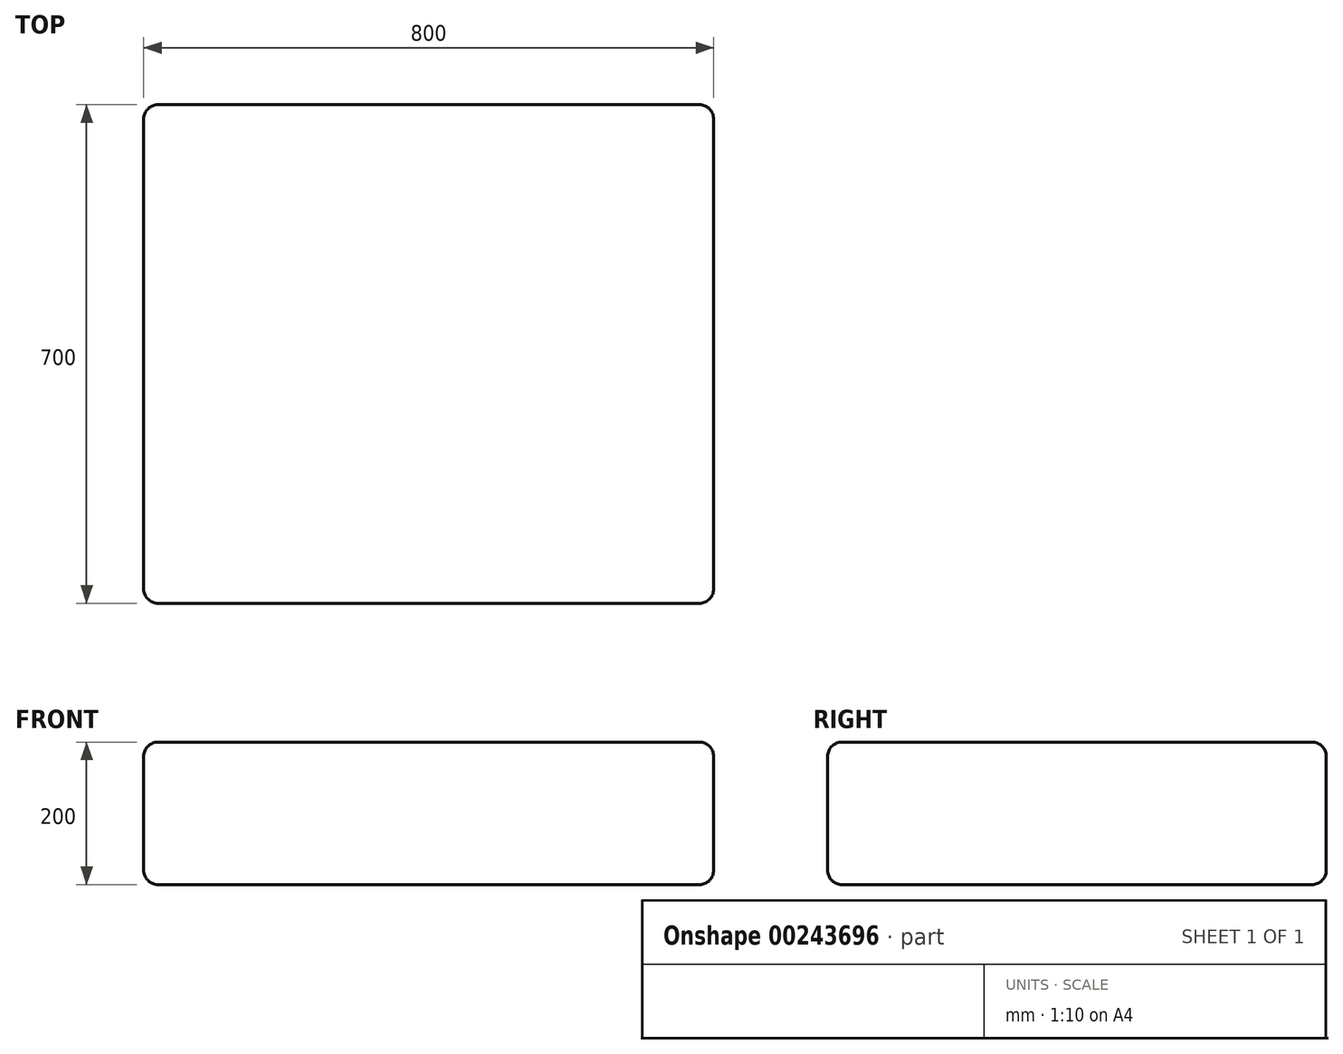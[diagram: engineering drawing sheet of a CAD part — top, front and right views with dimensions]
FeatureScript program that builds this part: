
annotation { "Feature Type Name" : "Feature", "Feature Type Description" : "" }
export const myFeature = defineFeature(function(context is Context, id is Id, definition is map)
    precondition{}
    {
        {
            var Q0;
            Q0=qCreatedBy(makeId("Top.planeOp"),FACE);
            var sketch = newSketch(context, id + "F0", { "sketchPlane" : qUnion([Q0])});
            skLineSegment(sketch, "E0.bottom", {"start": v(-400, 350) * mm, "end": v(400, 350) * mm});
            skLineSegment(sketch, "E0.top", {"start": v(-400, -350) * mm, "end": v(400, -350) * mm});
            skLineSegment(sketch, "E0.left", {"start": v(-400, 350) * mm, "end": v(-400, -350) * mm});
            skLineSegment(sketch, "E0.right", {"start": v(400, 350) * mm, "end": v(400, -350) * mm});
            skLineSegment(sketch, "E1", {"start": v(0, 350) * mm, "end": v(0, -350) * mm, "construction": true});
            skLineSegment(sketch, "E2", {"start": v(-400, 0) * mm, "end": v(400, 0) * mm, "construction": true});
            skSolve(sketch);
        }
        {
            var Q0;
            Q0=makeQuery(id+"F0.imprint","IMPRINT",FACE,{"disambiguationData":[TD([[makeQuery(id+"F0.imprint","IMPRINT",EDGE,{"derivedFrom":sQuery(id+"F0.wireOp",EDGE,"E0.bottom")}),-1.0]])]});
            extrude(context, id + "F1", {"entities" : qUnion([Q0]), "endBound" : BoundingType.SYMMETRIC, "depth" : 200 * mm});
        }
        {
            var Q0;
            Q0=makeQuery(id+"F1.opExtrude","SWEPT_EDGE",EDGE,{"disambiguationData":[OSD([sQuery(id+"F0.wireOp",EDGE,"E0.top"),sQuery(id+"F0.wireOp",EDGE,"E0.left")])]});
            var Q1;
            Q1=makeQuery(id+"F1.opExtrude","SWEPT_EDGE",EDGE,{"disambiguationData":[OSD([sQuery(id+"F0.wireOp",EDGE,"E0.top"),sQuery(id+"F0.wireOp",EDGE,"E0.right")])]});
            var Q2;
            Q2=makeQuery(id+"F1.opExtrude","SWEPT_EDGE",EDGE,{"disambiguationData":[OSD([sQuery(id+"F0.wireOp",EDGE,"E0.bottom"),sQuery(id+"F0.wireOp",EDGE,"E0.right")])]});
            var Q3;
            Q3=makeQuery(id+"F1.opExtrude","SWEPT_EDGE",EDGE,{"disambiguationData":[OSD([sQuery(id+"F0.wireOp",EDGE,"E0.bottom"),sQuery(id+"F0.wireOp",EDGE,"E0.left")])]});
            var Q4;
            Q4=makeQuery(id+"F1.opExtrude","CAP_EDGE",EDGE,{"disambiguationData":[OSD([sQuery(id+"F0.wireOp",EDGE,"E0.left")])],"isStart":false});
            var Q5;
            Q5=makeQuery(id+"F1.opExtrude","CAP_EDGE",EDGE,{"disambiguationData":[OSD([sQuery(id+"F0.wireOp",EDGE,"E0.top")])],"isStart":false});
            var Q6;
            Q6=makeQuery(id+"F1.opExtrude","CAP_EDGE",EDGE,{"disambiguationData":[OSD([sQuery(id+"F0.wireOp",EDGE,"E0.right")])],"isStart":false});
            var Q7;
            Q7=makeQuery(id+"F1.opExtrude","CAP_EDGE",EDGE,{"disambiguationData":[OSD([sQuery(id+"F0.wireOp",EDGE,"E0.bottom")])],"isStart":false});
            var Q8;
            Q8=makeQuery(id+"F1.opExtrude","CAP_EDGE",EDGE,{"disambiguationData":[OSD([sQuery(id+"F0.wireOp",EDGE,"E0.top")])],"isStart":true});
            var Q9;
            Q9=makeQuery(id+"F1.opExtrude","CAP_EDGE",EDGE,{"disambiguationData":[OSD([sQuery(id+"F0.wireOp",EDGE,"E0.right")])],"isStart":true});
            var Q10;
            Q10=makeQuery(id+"F1.opExtrude","CAP_EDGE",EDGE,{"disambiguationData":[OSD([sQuery(id+"F0.wireOp",EDGE,"E0.bottom")])],"isStart":true});
            var Q11;
            Q11=makeQuery(id+"F1.opExtrude","CAP_EDGE",EDGE,{"disambiguationData":[OSD([sQuery(id+"F0.wireOp",EDGE,"E0.left")])],"isStart":true});
            fillet(context, id + "F2", {"entities" : qUnion([Q0, Q1, Q2, Q3, Q4, Q5, Q6, Q7, Q8, Q9, Q10, Q11]), "radius" : 20 * mm, "tangentPropagation" : true, "allowEdgeOverflow" : false});
        }
    });
